# Revit family: HM-17
name_source: partatom
category: Aparatos sanitarios
units: mm (PartAtom-declared; Revit-internal decimal feet)

## family parameters
Compartido = No
Corte con vacíos al cargar = No
Cota de conector redondo = Diámetro de uso
Número OmniClass = 23.45.00.00
Punto de cálculo de habitación = No
Se basa en plano de trabajo = No
Siempre vertical = Sí
Tipo de pieza = Normal
Título OmniClass = Sanitary, Laundry, and Cleaning Equipment

## types (1)
- HM-17
    Brass Chromed = Brass
    Comentarios de tipo = Lavatory Faucet Assemblies
    Data Sheet = http://www.helvex.com.mx
    Descripción = Faucet Albatros 4" With Grid Drain
    Elevación por defecto = 0"
    Fabricante = HELVEX
    Features = Valvex II Left And Right ¼ Turn Ceramic Discs; Includes Setting Kit; Automatic Drain With Overflow
    Inlet Threads = ½" - 14 NPSM
    Instructive = http://www.helvex.com.mx
    Max. Working Pressure = 85.3 psi
    Min. Working Pressure = 3.5 psi
    Modelo = HM-17
    Total Height = 5"
    Total Length = 6"
    Total Width = 4"
    URL = http://www.helvex.com.mx

## geometry (parser evidence)
native form markers: Sweep x3
no freeform markers — native parametric forms only
